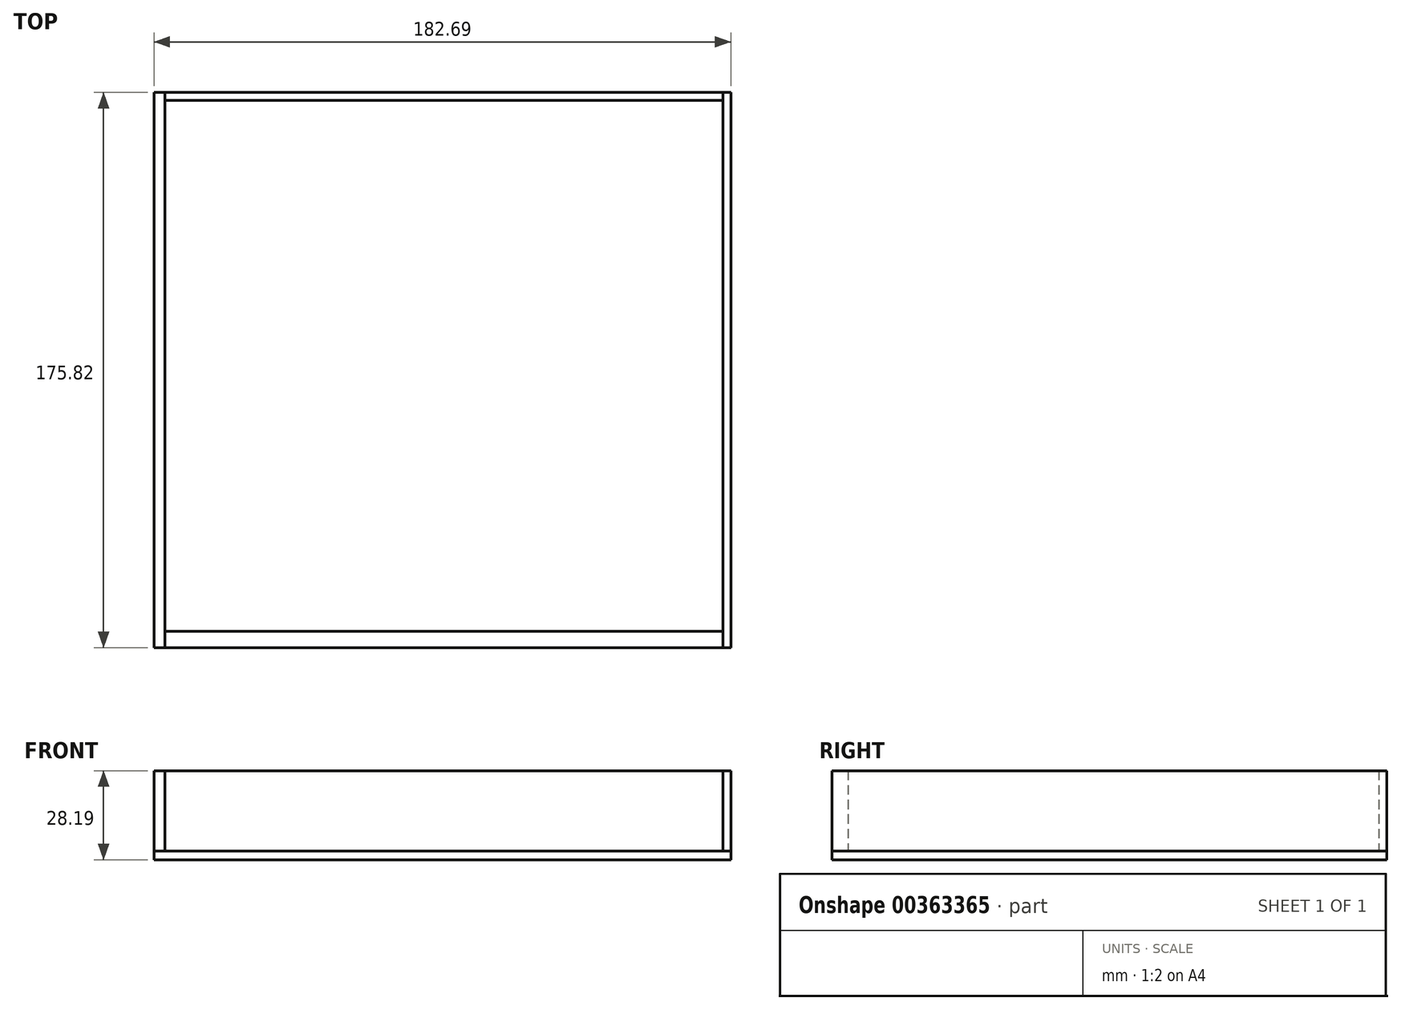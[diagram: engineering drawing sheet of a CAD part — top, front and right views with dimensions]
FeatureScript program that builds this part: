
annotation { "Feature Type Name" : "Feature", "Feature Type Description" : "" }
export const myFeature = defineFeature(function(context is Context, id is Id, definition is map)
    precondition{}
    {
        {
            var Q0;
            Q0=qCreatedBy(makeId("Top.planeOp"),FACE);
            var sketch = newSketch(context, id + "F0", { "sketchPlane" : qUnion([Q0])});
            skLineSegment(sketch, "E0.bottom", {"start": v(-112.61, 39.11) * mm, "end": v(70.08, 39.11) * mm});
            skLineSegment(sketch, "E0.top", {"start": v(-112.61, -136.7) * mm, "end": v(70.08, -136.7) * mm});
            skLineSegment(sketch, "E0.left", {"start": v(-112.61, 39.11) * mm, "end": v(-112.61, -136.7) * mm});
            skLineSegment(sketch, "E0.right", {"start": v(70.08, 39.11) * mm, "end": v(70.08, -136.7) * mm});
            skSolve(sketch);
        }
        {
            var Q0;
            Q0=makeQuery(id+"F0.imprint","IMPRINT",FACE,{"disambiguationData":[TD([[makeQuery(id+"F0.imprint","IMPRINT",EDGE,{"derivedFrom":sQuery(id+"F0.wireOp",EDGE,"E0.bottom")}),-1.0]])]});
            extrude(context, id + "F1", {"entities" : qUnion([Q0]), "depth" : 2.8 * mm});
        }
        {
            var Q0;
            Q0=makeQuery(id+"F1.opExtrude","CAP_FACE",FACE,{"disambiguationData":[OSD([sQuery(id+"F0.wireOp",EDGE,"E0.bottom"),sQuery(id+"F0.wireOp",EDGE,"E0.top"),sQuery(id+"F0.wireOp",EDGE,"E0.left"),sQuery(id+"F0.wireOp",EDGE,"E0.right")])],"isStart":false});
            var sketch = newSketch(context, id + "F2", { "sketchPlane" : qUnion([Q0])});
            skLineSegment(sketch, "E1.bottom", {"start": v(70.08, 39.11) * mm, "end": v(67.54, 39.11) * mm});
            skLineSegment(sketch, "E1.top", {"start": v(70.08, -136.7) * mm, "end": v(67.54, -136.7) * mm});
            skLineSegment(sketch, "E1.left", {"start": v(70.08, 39.11) * mm, "end": v(70.08, -136.7) * mm});
            skLineSegment(sketch, "E1.right", {"start": v(67.54, 39.11) * mm, "end": v(67.54, -136.7) * mm});
            skSolve(sketch);
        }
        {
            var Q0;
            Q0 = qSketchRegion(id + "F2", true);
            extrude(context, id + "F3", {"entities" : qUnion([Q0]), "depth" : 25.4 * mm});
        }
        {
            var Q0;
            Q0=makeQuery(id+"F1.opExtrude","CAP_FACE",FACE,{"disambiguationData":[OSD([sQuery(id+"F0.wireOp",EDGE,"E0.bottom"),sQuery(id+"F0.wireOp",EDGE,"E0.top"),sQuery(id+"F0.wireOp",EDGE,"E0.left"),sQuery(id+"F0.wireOp",EDGE,"E0.right")])],"isStart":false});
            var sketch = newSketch(context, id + "F4", { "sketchPlane" : qUnion([Q0])});
            skLineSegment(sketch, "E2.bottom", {"start": v(-112.61, 39.11) * mm, "end": v(-109.2, 39.11) * mm});
            skLineSegment(sketch, "E2.top", {"start": v(-112.61, -136.7) * mm, "end": v(-109.2, -136.7) * mm});
            skLineSegment(sketch, "E2.left", {"start": v(-112.61, 39.11) * mm, "end": v(-112.61, -136.7) * mm});
            skLineSegment(sketch, "E2.right", {"start": v(-109.2, 39.11) * mm, "end": v(-109.2, -136.7) * mm});
            skSolve(sketch);
        }
        {
            var Q0;
            Q0=makeQuery(id+"F4.imprint","IMPRINT",FACE,{"disambiguationData":[TD([[makeQuery(id+"F4.imprint","IMPRINT",EDGE,{"derivedFrom":sQuery(id+"F4.wireOp",EDGE,"E2.bottom")}),-1.0]])]});
            extrude(context, id + "F5", {"entities" : qUnion([Q0]), "depth" : 25.4 * mm});
        }
        {
            var Q0;
            Q0=makeQuery(id+"F1.opExtrude","CAP_FACE",FACE,{"disambiguationData":[OSD([sQuery(id+"F0.wireOp",EDGE,"E0.bottom"),sQuery(id+"F0.wireOp",EDGE,"E0.top"),sQuery(id+"F0.wireOp",EDGE,"E0.left"),sQuery(id+"F0.wireOp",EDGE,"E0.right")])],"isStart":false});
            var sketch = newSketch(context, id + "F6", { "sketchPlane" : qUnion([Q0])});
            skSolve(sketch);
        }
        {
            var Q0;
            Q0=makeQuery(id+"F6.imprint","IMPRINT",FACE,{"disambiguationData":[TD([[makeQuery(id+"F6.imprint","IMPRINT",EDGE,{"derivedFrom":makeQuery(id+"F1.opExtrude","CAP_EDGE",EDGE,{"disambiguationData":[OSD([sQuery(id+"F0.wireOp",EDGE,"E0.bottom")])],"isStart":false})}),-1.0]])]});
            var sketch = newSketch(context, id + "F7", { "sketchPlane" : qUnion([Q0])});
            skLineSegment(sketch, "E3.bottom", {"start": v(-109.2, -136.7) * mm, "end": v(67.54, -136.7) * mm});
            skLineSegment(sketch, "E3.top", {"start": v(-109.2, -131.57) * mm, "end": v(67.54, -131.57) * mm});
            skLineSegment(sketch, "E3.left", {"start": v(-109.2, -136.7) * mm, "end": v(-109.2, -131.57) * mm});
            skLineSegment(sketch, "E3.right", {"start": v(67.54, -136.7) * mm, "end": v(67.54, -131.57) * mm});
            skSolve(sketch);
        }
        {
            var Q0;
            Q0=makeQuery(id+"F7.imprint","IMPRINT",FACE,{"disambiguationData":[TD([[makeQuery(id+"F7.imprint","IMPRINT",EDGE,{"derivedFrom":sQuery(id+"F7.wireOp",EDGE,"E3.bottom")}),1.0]])]});
            extrude(context, id + "F8", {"entities" : qUnion([Q0]), "depth" : 25.4 * mm});
        }
        {
            var Q0;
            Q0=makeQuery(id+"F6.imprint","IMPRINT",FACE,{"disambiguationData":[TD([[makeQuery(id+"F6.imprint","IMPRINT",EDGE,{"derivedFrom":makeQuery(id+"F1.opExtrude","CAP_EDGE",EDGE,{"disambiguationData":[OSD([sQuery(id+"F0.wireOp",EDGE,"E0.bottom")])],"isStart":false})}),-1.0]])]});
            var sketch = newSketch(context, id + "F9", { "sketchPlane" : qUnion([Q0])});
            skLineSegment(sketch, "E4.bottom", {"start": v(-109.2, 36.57) * mm, "end": v(67.54, 36.57) * mm});
            skLineSegment(sketch, "E4.top", {"start": v(-109.2, 39.11) * mm, "end": v(67.54, 39.11) * mm});
            skLineSegment(sketch, "E4.left", {"start": v(-109.2, 36.57) * mm, "end": v(-109.2, 39.11) * mm});
            skLineSegment(sketch, "E4.right", {"start": v(67.54, 36.57) * mm, "end": v(67.54, 39.11) * mm});
            skSolve(sketch);
        }
        {
            var Q0;
            Q0=makeQuery(id+"F9.imprint","IMPRINT",FACE,{"disambiguationData":[TD([[makeQuery(id+"F9.imprint","IMPRINT",EDGE,{"derivedFrom":sQuery(id+"F9.wireOp",EDGE,"E4.bottom")}),1.0]])]});
            extrude(context, id + "F10", {"entities" : qUnion([Q0]), "depth" : 25.4 * mm});
        }
    });
